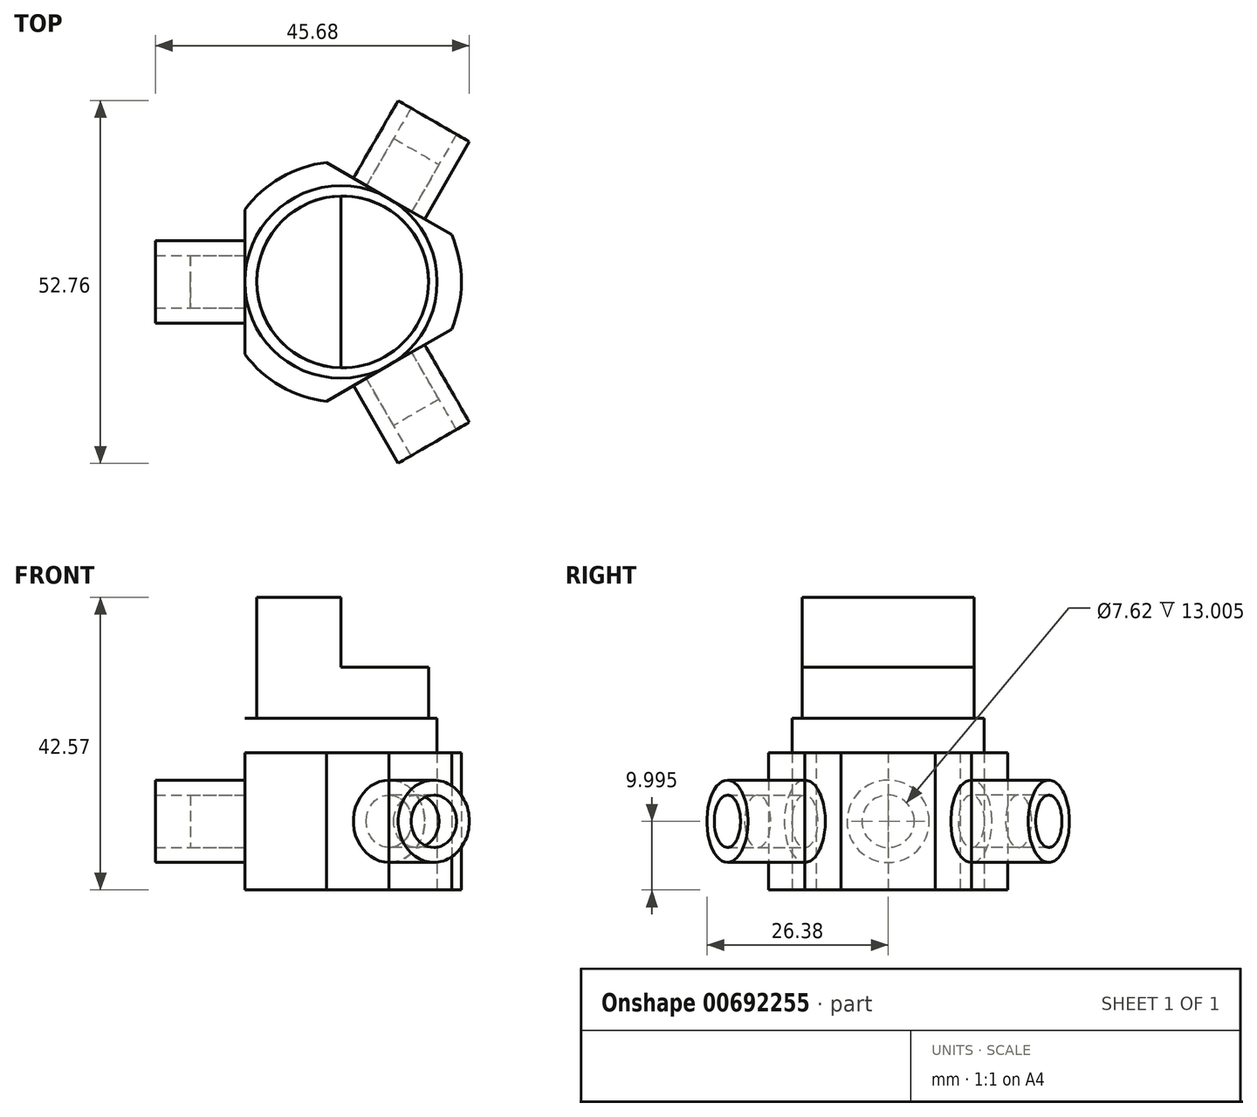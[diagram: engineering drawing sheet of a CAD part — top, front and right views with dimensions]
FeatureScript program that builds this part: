
annotation { "Feature Type Name" : "Feature", "Feature Type Description" : "" }
export const myFeature = defineFeature(function(context is Context, id is Id, definition is map)
    precondition{}
    {
        {
            var Q0;
            Q0=qCreatedBy(makeId("Top.planeOp"),FACE);
            var sketch = newSketch(context, id + "F0", { "sketchPlane" : qUnion([Q0])});
            skLineSegment(sketch, "E0", {"start": v(-14, -10.5) * mm, "end": v(-14, 10.5) * mm});
            skLineSegment(sketch, "E1", {"start": v(-14, 10.5) * mm, "end": v(-2.1, 17.37) * mm});
            skLineSegment(sketch, "E2", {"start": v(16.1, -6.87) * mm, "end": v(-2.1, -17.37) * mm});
            skLineSegment(sketch, "E3", {"start": v(-2.1, -17.37) * mm, "end": v(-14, -10.5) * mm});
            skLineSegment(sketch, "E4", {"start": v(-2.1, 17.37) * mm, "end": v(16.1, 6.87) * mm});
            skLineSegment(sketch, "E5", {"start": v(16.1, 6.87) * mm, "end": v(16.1, -6.87) * mm});
            skCircle(sketch, "E6", {"center": v(0, 0) * mm, "radius": 14 * mm});
            skArc(sketch, "E7", {"start": v(-2.1, 17.37) * mm, "mid": v(-8.76, 15.17) * mm, "end": v(-14, 10.5) * mm});
            skArc(sketch, "E8", {"start": v(16.1, -6.87) * mm, "mid": v(17.52, 0) * mm, "end": v(16.1, 6.87) * mm});
            skArc(sketch, "E9", {"start": v(-14, -10.5) * mm, "mid": v(-8.76, -15.17) * mm, "end": v(-2.1, -17.37) * mm});
            skCircle(sketch, "E10", {"center": v(0.25, 0) * mm, "radius": 12.5 * mm});
            skSolve(sketch);
        }
        {
            var Q0;
            {var subQ1=sQuery(id+"F0.wireOp",EDGE,"E3");Q0=makeQuery(id+"F0.imprint","IMPRINT",FACE,{"disambiguationData":[TD([[makeQuery(id+"F0.imprint","IMPRINT",EDGE,{"derivedFrom":subQ1}),-1.0]])]});}
            var Q1;
            Q1=makeQuery(id+"F0.imprint","IMPRINT",FACE,{"disambiguationData":[TD([[makeQuery(id+"F0.imprint","IMPRINT",EDGE,{"derivedFrom":sQuery(id+"F0.wireOp",EDGE,"E3")}),1.0]])]});
            var Q2;
            Q2=makeQuery(id+"F0.imprint","IMPRINT",FACE,{"disambiguationData":[TD([[makeQuery(id+"F0.imprint","IMPRINT",EDGE,{"derivedFrom":sQuery(id+"F0.wireOp",EDGE,"E1")}),1.0]])]});
            var Q3;
            {var subQ1=sQuery(id+"F0.wireOp",EDGE,"E1");Q3=makeQuery(id+"F0.imprint","IMPRINT",FACE,{"disambiguationData":[TD([[makeQuery(id+"F0.imprint","IMPRINT",EDGE,{"derivedFrom":subQ1}),-1.0]])]});}
            var Q4;
            {var subQ1=sQuery(id+"F0.wireOp",EDGE,"E5");Q4=makeQuery(id+"F0.imprint","IMPRINT",FACE,{"disambiguationData":[TD([[makeQuery(id+"F0.imprint","IMPRINT",EDGE,{"derivedFrom":subQ1}),-1.0]])]});}
            var Q5;
            Q5=makeQuery(id+"F0.imprint","IMPRINT",FACE,{"disambiguationData":[TD([[makeQuery(id+"F0.imprint","IMPRINT",EDGE,{"derivedFrom":sQuery(id+"F0.wireOp",EDGE,"E5")}),1.0]])]});
            extrude(context, id + "F1", {"entities" : qUnion([Q0, Q1, Q2, Q3, Q4, Q5]), "depth" : 19.99 * mm, "offsetDistance" : 25.4 * mm});
        }
        {
            var Q0;
            {var subQ0=sQuery(id+"F0.wireOp",EDGE,"E6");var subQ1=makeQuery(id+"F0.imprint","INTERSECT",VERTEX,{"derivedFrom":[sQuery(id+"F0.wireOp",EDGE,"E0"),subQ0]});Q0=makeQuery(id+"F0.imprint","IMPRINT",FACE,{"disambiguationData":[TD([[makeQuery(id+"F0.imprint","IMPRINT",EDGE,{"disambiguationData":[TD([[subQ1,1.0]])],"derivedFrom":subQ0}),1.0]])]});}
            extrude(context, id + "F2", {"entities" : qUnion([Q0]), "depth" : 25 * mm, "offsetDistance" : 25.4 * mm});
        }
        {
            var Q0;
            Q0=makeQuery(id+"F0.imprint","IMPRINT",FACE,{"disambiguationData":[TD([[makeQuery(id+"F0.imprint","IMPRINT",EDGE,{"derivedFrom":sQuery(id+"F0.wireOp",EDGE,"E10")}),1.0]])]});
            extrude(context, id + "F3", {"entities" : qUnion([Q0]), "operationType" : NewBodyOperationType.ADD, "depth" : 37.5 * mm, "offsetDistance" : 25.4 * mm});
        }
        {
            var Q0;
            {var subQ0=sQuery(id+"F0.wireOp",EDGE,"E0");Q0=makeQuery(id+"F1.opExtrude","SWEPT_FACE",FACE,{"disambiguationData":[OSD([subQ0]),TDD([makeQuery(id+"F0.imprint","IMPRINT",EDGE,{"disambiguationData":[TD([[makeQuery(id+"F0.imprint","INTERSECT",VERTEX,{"derivedFrom":[subQ0,sQuery(id+"F0.wireOp",EDGE,"E6")]}),-1.0]])],"derivedFrom":subQ0})])]});}
            var sketch = newSketch(context, id + "F4", { "sketchPlane" : qUnion([Q0])});
            skCircle(sketch, "E11", {"center": v(0, 10) * mm, "radius": 5.98 * mm});
            skCircle(sketch, "E12", {"center": v(0, 10) * mm, "radius": 3.81 * mm});
            skSolve(sketch);
        }
        {
            var Q0;
            {var subQ0=sQuery(id+"F4.wireOp",EDGE,"E11");var subQ1=makeQuery(id+"F1.opExtrude","SWEPT_EDGE",EDGE,{"disambiguationData":[OSD([sQuery(id+"F0.wireOp",EDGE,"E0"),sQuery(id+"F0.wireOp",EDGE,"E6")]),OD(1.0)]});var subQ2=makeQuery(id+"F4.imprint","INTERSECT",VERTEX,{"disambiguationData":[OD(0.0)],"derivedFrom":[subQ1,subQ0]});Q0=makeQuery(id+"F4.imprint","IMPRINT",FACE,{"disambiguationData":[TD([[makeQuery(id+"F4.imprint","IMPRINT",EDGE,{"disambiguationData":[TD([[subQ2,-1.0]])],"derivedFrom":subQ0}),1.0]])]});}
            var Q1;
            {var subQ0=sQuery(id+"F4.wireOp",EDGE,"E11");var subQ1=makeQuery(id+"F1.opExtrude","SWEPT_EDGE",EDGE,{"disambiguationData":[OSD([sQuery(id+"F0.wireOp",EDGE,"E0"),sQuery(id+"F0.wireOp",EDGE,"E6")]),OD(1.0)]});var subQ2=makeQuery(id+"F4.imprint","INTERSECT",VERTEX,{"disambiguationData":[OD(0.0)],"derivedFrom":[subQ1,subQ0]});Q1=makeQuery(id+"F4.imprint","IMPRINT",FACE,{"disambiguationData":[TD([[makeQuery(id+"F4.imprint","IMPRINT",EDGE,{"disambiguationData":[TD([[subQ2,1.0]])],"derivedFrom":subQ0}),1.0]])]});}
            extrude(context, id + "F5", {"entities" : qUnion([Q0, Q1]), "depth" : 13 * mm, "offsetDistance" : 25.4 * mm});
        }
        {
            var Q0;
            {var subQ0=sQuery(id+"F0.wireOp",EDGE,"E2");Q0=makeQuery(id+"F1.opExtrude","SWEPT_FACE",FACE,{"disambiguationData":[OSD([subQ0]),TDD([makeQuery(id+"F0.imprint","IMPRINT",EDGE,{"disambiguationData":[TD([[makeQuery(id+"F0.imprint","INTERSECT",VERTEX,{"derivedFrom":[subQ0,sQuery(id+"F0.wireOp",EDGE,"E6")]}),-1.0]])],"derivedFrom":subQ0})])]});}
            var sketch = newSketch(context, id + "F6", { "sketchPlane" : qUnion([Q0])});
            skCircle(sketch, "E13", {"center": v(0, 10) * mm, "radius": 5.98 * mm});
            skCircle(sketch, "E14", {"center": v(0, 10) * mm, "radius": 3.81 * mm});
            skSolve(sketch);
        }
        {
            var Q0;
            Q0 = qSketchRegion(id + "F6", true);
            extrude(context, id + "F7", {"entities" : qUnion([Q0]), "depth" : 13 * mm, "offsetDistance" : 25.4 * mm});
        }
        {
            var Q0;
            {var subQ0=sQuery(id+"F4.wireOp",EDGE,"E12");var subQ1=makeQuery(id+"F1.opExtrude","SWEPT_EDGE",EDGE,{"disambiguationData":[OSD([sQuery(id+"F0.wireOp",EDGE,"E0"),sQuery(id+"F0.wireOp",EDGE,"E6")]),OD(1.0)]});var subQ2=makeQuery(id+"F4.imprint","INTERSECT",VERTEX,{"disambiguationData":[OD(0.0)],"derivedFrom":[subQ1,subQ0]});Q0=makeQuery(id+"F4.imprint","IMPRINT",FACE,{"disambiguationData":[TD([[makeQuery(id+"F4.imprint","IMPRINT",EDGE,{"disambiguationData":[TD([[subQ2,1.0]])],"derivedFrom":subQ0}),1.0]])]});}
            var Q1;
            {var subQ0=sQuery(id+"F4.wireOp",EDGE,"E12");var subQ1=makeQuery(id+"F1.opExtrude","SWEPT_EDGE",EDGE,{"disambiguationData":[OSD([sQuery(id+"F0.wireOp",EDGE,"E0"),sQuery(id+"F0.wireOp",EDGE,"E6")]),OD(1.0)]});var subQ2=makeQuery(id+"F4.imprint","INTERSECT",VERTEX,{"disambiguationData":[OD(0.0)],"derivedFrom":[subQ1,subQ0]});Q1=makeQuery(id+"F4.imprint","IMPRINT",FACE,{"disambiguationData":[TD([[makeQuery(id+"F4.imprint","IMPRINT",EDGE,{"disambiguationData":[TD([[subQ2,-1.0]])],"derivedFrom":subQ0}),1.0]])]});}
            extrude(context, id + "F8", {"entities" : qUnion([Q0, Q1]), "depth" : 7.92 * mm, "offsetDistance" : 25.4 * mm});
        }
        {
            var Q0;
            {var subQ0=sQuery(id+"F6.wireOp",EDGE,"E14");var subQ1=makeQuery(id+"F1.opExtrude","SWEPT_EDGE",EDGE,{"disambiguationData":[OSD([sQuery(id+"F0.wireOp",EDGE,"E2"),sQuery(id+"F0.wireOp",EDGE,"E6")]),OD(1.0)]});var subQ2=makeQuery(id+"F6.imprint","INTERSECT",VERTEX,{"disambiguationData":[OD(0.0)],"derivedFrom":[subQ1,subQ0]});Q0=makeQuery(id+"F6.imprint","IMPRINT",FACE,{"disambiguationData":[TD([[makeQuery(id+"F6.imprint","IMPRINT",EDGE,{"disambiguationData":[TD([[subQ2,1.0]])],"derivedFrom":subQ0}),1.0]])]});}
            var Q1;
            {var subQ0=sQuery(id+"F6.wireOp",EDGE,"E14");var subQ1=makeQuery(id+"F1.opExtrude","SWEPT_EDGE",EDGE,{"disambiguationData":[OSD([sQuery(id+"F0.wireOp",EDGE,"E2"),sQuery(id+"F0.wireOp",EDGE,"E6")]),OD(1.0)]});var subQ2=makeQuery(id+"F6.imprint","INTERSECT",VERTEX,{"disambiguationData":[OD(0.0)],"derivedFrom":[subQ1,subQ0]});Q1=makeQuery(id+"F6.imprint","IMPRINT",FACE,{"disambiguationData":[TD([[makeQuery(id+"F6.imprint","IMPRINT",EDGE,{"disambiguationData":[TD([[subQ2,-1.0]])],"derivedFrom":subQ0}),1.0]])]});}
            extrude(context, id + "F9", {"entities" : qUnion([Q0, Q1]), "depth" : 7.92 * mm, "offsetDistance" : 25.4 * mm});
        }
        {
            var Q0;
            {var subQ0=sQuery(id+"F0.wireOp",EDGE,"E4");Q0=makeQuery(id+"F1.opExtrude","SWEPT_FACE",FACE,{"disambiguationData":[OSD([subQ0]),TDD([makeQuery(id+"F0.imprint","IMPRINT",EDGE,{"disambiguationData":[TD([[makeQuery(id+"F0.imprint","INTERSECT",VERTEX,{"derivedFrom":[subQ0,sQuery(id+"F0.wireOp",EDGE,"E6")]}),-1.0]])],"derivedFrom":subQ0})])]});}
            var sketch = newSketch(context, id + "F10", { "sketchPlane" : qUnion([Q0])});
            skCircle(sketch, "E15", {"center": v(0, 10) * mm, "radius": 5.98 * mm});
            skCircle(sketch, "E16", {"center": v(0, 10) * mm, "radius": 3.81 * mm});
            skSolve(sketch);
        }
        {
            var Q0;
            {var subQ0=sQuery(id+"F10.wireOp",EDGE,"E15");var subQ1=makeQuery(id+"F1.opExtrude","SWEPT_EDGE",EDGE,{"disambiguationData":[OSD([sQuery(id+"F0.wireOp",EDGE,"E4"),sQuery(id+"F0.wireOp",EDGE,"E6")]),OD(1.0)]});var subQ2=makeQuery(id+"F10.imprint","INTERSECT",VERTEX,{"disambiguationData":[OD(0.0)],"derivedFrom":[subQ1,subQ0]});Q0=makeQuery(id+"F10.imprint","IMPRINT",FACE,{"disambiguationData":[TD([[makeQuery(id+"F10.imprint","IMPRINT",EDGE,{"disambiguationData":[TD([[subQ2,1.0]])],"derivedFrom":subQ0}),1.0]])]});}
            var Q1;
            {var subQ0=sQuery(id+"F10.wireOp",EDGE,"E15");var subQ1=makeQuery(id+"F1.opExtrude","SWEPT_EDGE",EDGE,{"disambiguationData":[OSD([sQuery(id+"F0.wireOp",EDGE,"E4"),sQuery(id+"F0.wireOp",EDGE,"E6")]),OD(1.0)]});var subQ2=makeQuery(id+"F10.imprint","INTERSECT",VERTEX,{"disambiguationData":[OD(0.0)],"derivedFrom":[subQ1,subQ0]});Q1=makeQuery(id+"F10.imprint","IMPRINT",FACE,{"disambiguationData":[TD([[makeQuery(id+"F10.imprint","IMPRINT",EDGE,{"disambiguationData":[TD([[subQ2,-1.0]])],"derivedFrom":subQ0}),1.0]])]});}
            extrude(context, id + "F11", {"entities" : qUnion([Q0, Q1]), "depth" : 13 * mm, "offsetDistance" : 25.4 * mm});
        }
        {
            var Q0;
            {var subQ0=sQuery(id+"F10.wireOp",EDGE,"E16");var subQ1=makeQuery(id+"F1.opExtrude","SWEPT_EDGE",EDGE,{"disambiguationData":[OSD([sQuery(id+"F0.wireOp",EDGE,"E4"),sQuery(id+"F0.wireOp",EDGE,"E6")]),OD(1.0)]});var subQ2=makeQuery(id+"F10.imprint","INTERSECT",VERTEX,{"disambiguationData":[OD(0.0)],"derivedFrom":[subQ1,subQ0]});Q0=makeQuery(id+"F10.imprint","IMPRINT",FACE,{"disambiguationData":[TD([[makeQuery(id+"F10.imprint","IMPRINT",EDGE,{"disambiguationData":[TD([[subQ2,-1.0]])],"derivedFrom":subQ0}),1.0]])]});}
            var Q1;
            {var subQ0=sQuery(id+"F10.wireOp",EDGE,"E16");var subQ1=makeQuery(id+"F1.opExtrude","SWEPT_EDGE",EDGE,{"disambiguationData":[OSD([sQuery(id+"F0.wireOp",EDGE,"E4"),sQuery(id+"F0.wireOp",EDGE,"E6")]),OD(1.0)]});var subQ2=makeQuery(id+"F10.imprint","INTERSECT",VERTEX,{"disambiguationData":[OD(0.0)],"derivedFrom":[subQ1,subQ0]});Q1=makeQuery(id+"F10.imprint","IMPRINT",FACE,{"disambiguationData":[TD([[makeQuery(id+"F10.imprint","IMPRINT",EDGE,{"disambiguationData":[TD([[subQ2,1.0]])],"derivedFrom":subQ0}),1.0]])]});}
            extrude(context, id + "F12", {"entities" : qUnion([Q0, Q1]), "depth" : 7.92 * mm, "offsetDistance" : 25.4 * mm});
        }
        {
            var Q0;
            Q0=makeQuery(id+"F3.opExtrude","CAP_FACE",FACE,{"disambiguationData":[OSD([sQuery(id+"F0.wireOp",EDGE,"E10")])],"isStart":false});
            var sketch = newSketch(context, id + "F13", { "sketchPlane" : qUnion([Q0])});
            skLineSegment(sketch, "E17", {"start": v(0, -12.5) * mm, "end": v(0, 12.5) * mm});
            skSolve(sketch);
        }
        {
            var Q0;
            Q0 = qSketchRegion(id + "F13", true);
            var Q1;
            {var subQ0=sQuery(id+"F13.wireOp",EDGE,"E17");Q1=makeQuery(id+"F13.imprint","IMPRINT",FACE,{"disambiguationData":[TD([[makeQuery(id+"F13.imprint","IMPRINT",EDGE,{"derivedFrom":subQ0}),1.0]])]});}
            extrude(context, id + "F14", {"entities" : qUnion([Q0, Q1]), "operationType" : NewBodyOperationType.ADD, "depth" : 5.08 * mm, "offsetDistance" : 25.4 * mm});
        }
        {
            var Q0;
            Q0=makeQuery(id+"F3.opExtrude","CAP_FACE",FACE,{"disambiguationData":[OSD([sQuery(id+"F0.wireOp",EDGE,"E10")])],"isStart":false});
            extrude(context, id + "F15", {"entities" : qUnion([Q0]), "operationType" : NewBodyOperationType.REMOVE, "oppositeDirection" : true, "depth" : 5.08 * mm, "offsetDistance" : 25.4 * mm});
        }
    });
